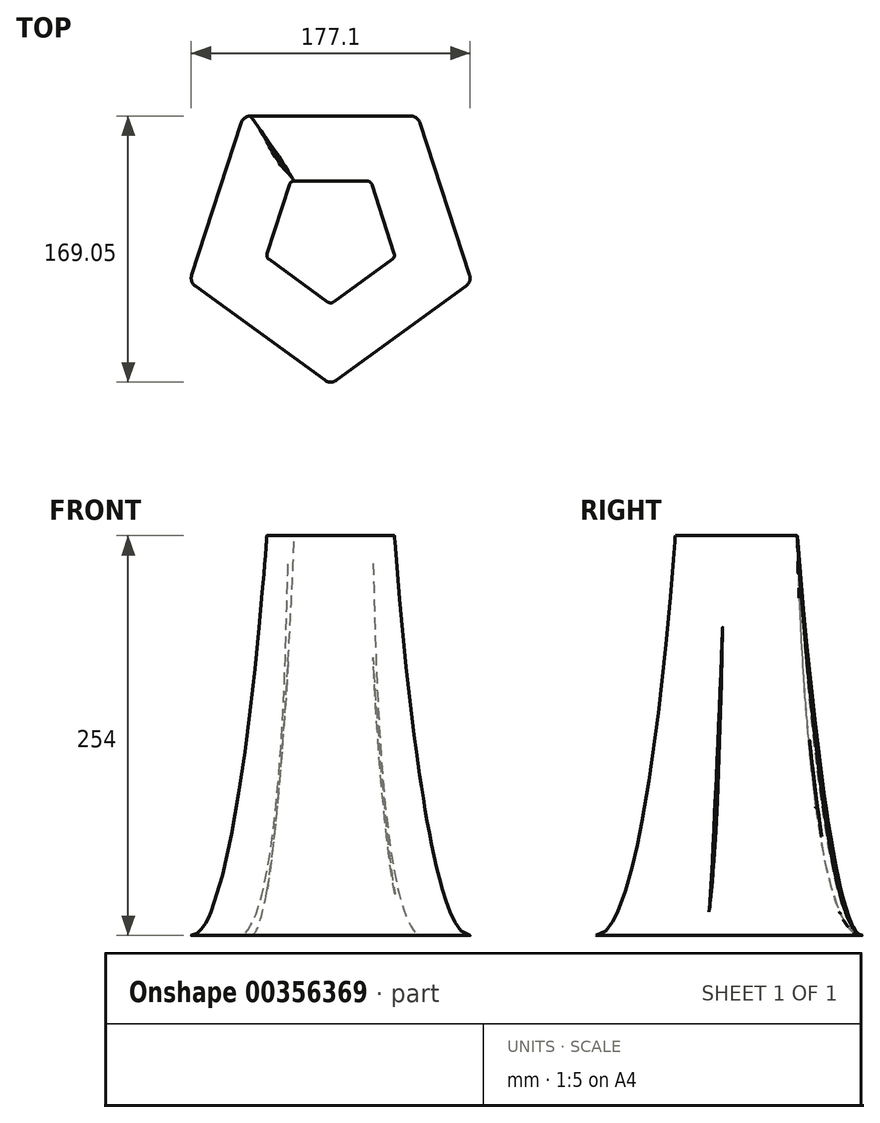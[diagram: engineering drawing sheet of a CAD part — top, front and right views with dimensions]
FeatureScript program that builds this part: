
annotation { "Feature Type Name" : "Feature", "Feature Type Description" : "" }
export const myFeature = defineFeature(function(context is Context, id is Id, definition is map)
    precondition{}
    {
        {
            var Q0;
            Q0=qCreatedBy(makeId("Top.planeOp"),FACE);
            var sketch = newSketch(context, id + "F0", { "sketchPlane" : qUnion([Q0])});
            skCircle(sketch, "E0.cCircle", {"center": v(0, 0) * mm, "radius": 76.27 * mm, "construction": true});
            skLineSegment(sketch, "E0.0", {"start": v(-50.8, 76.27) * mm, "end": v(50.8, 76.27) * mm});
            skLineSegment(sketch, "E0.1", {"start": v(56.84, 71.88) * mm, "end": v(88.24, -24.74) * mm});
            skLineSegment(sketch, "E0.2", {"start": v(85.93, -31.84) * mm, "end": v(3.73, -91.56) * mm});
            skLineSegment(sketch, "E0.3", {"start": v(-3.73, -91.56) * mm, "end": v(-85.93, -31.84) * mm});
            skLineSegment(sketch, "E0.4", {"start": v(-88.24, -24.74) * mm, "end": v(-56.84, 71.88) * mm});
            skPoint(sketch, "E0.0.midPoint", {"position": v(0, 76.27) * mm});
            skPoint(sketch, "E1.visualSharp", {"position": v(-55.41, 76.27) * mm});
            skArc(sketch, "E1.filletArc", {"start": v(-50.8, 76.27) * mm, "mid": v(-54.53, 75.06) * mm, "end": v(-56.84, 71.88) * mm});
            skPoint(sketch, "E2.visualSharp", {"position": v(55.41, 76.27) * mm});
            skArc(sketch, "E2.filletArc", {"start": v(56.84, 71.88) * mm, "mid": v(54.53, 75.06) * mm, "end": v(50.8, 76.27) * mm});
            skPoint(sketch, "E3.visualSharp", {"position": v(89.66, -29.13) * mm});
            skArc(sketch, "E3.filletArc", {"start": v(85.93, -31.84) * mm, "mid": v(88.24, -28.67) * mm, "end": v(88.24, -24.74) * mm});
            skPoint(sketch, "E4.visualSharp", {"position": v(-89.66, -29.13) * mm});
            skArc(sketch, "E4.filletArc", {"start": v(-88.24, -24.74) * mm, "mid": v(-88.24, -28.67) * mm, "end": v(-85.93, -31.84) * mm});
            skPoint(sketch, "E5.visualSharp", {"position": v(0, -94.28) * mm});
            skArc(sketch, "E5.filletArc", {"start": v(-3.73, -91.56) * mm, "mid": v(0, -92.78) * mm, "end": v(3.73, -91.56) * mm});
            skSolve(sketch);
        }
        {
            var Q0;
            Q0=makeQuery(id+"F0.imprint","IMPRINT",FACE,{"disambiguationData":[TD([[makeQuery(id+"F0.imprint","IMPRINT",EDGE,{"derivedFrom":sQuery(id+"F0.wireOp",EDGE,"E0.0")}),-1.0]])]});
            cPlane(context, id + "F1", {"entities" : qUnion([Q0]), "cplaneType" : CPlaneType.OFFSET, "offset" : 254 * mm, "width" : 152.4 * mm, "height" : 152.4 * mm});
        }
        {
            var Q0;
            Q0=qCreatedBy(id+"F1.planeOp",FACE);
            var sketch = newSketch(context, id + "F2", { "sketchPlane" : qUnion([Q0])});
            skCircle(sketch, "E6.cCircle", {"center": v(0, 0) * mm, "radius": 34.96 * mm, "construction": true});
            skLineSegment(sketch, "E6.0", {"start": v(-23.1, 34.96) * mm, "end": v(23.1, 34.96) * mm});
            skLineSegment(sketch, "E6.1", {"start": v(26.11, 32.77) * mm, "end": v(40.39, -11.16) * mm});
            skLineSegment(sketch, "E6.2", {"start": v(39.23, -14.7) * mm, "end": v(1.87, -41.86) * mm});
            skLineSegment(sketch, "E6.3", {"start": v(-1.87, -41.86) * mm, "end": v(-39.23, -14.7) * mm});
            skLineSegment(sketch, "E6.4", {"start": v(-40.39, -11.16) * mm, "end": v(-26.11, 32.77) * mm});
            skPoint(sketch, "E6.0.midPoint", {"position": v(0, 34.96) * mm});
            skPoint(sketch, "E7.visualSharp", {"position": v(-41.1, -13.35) * mm});
            skArc(sketch, "E7.filletArc", {"start": v(-40.39, -11.16) * mm, "mid": v(-40.39, -13.12) * mm, "end": v(-39.23, -14.7) * mm});
            skPoint(sketch, "E8.visualSharp", {"position": v(0, -43.21) * mm});
            skArc(sketch, "E8.filletArc", {"start": v(-1.87, -41.86) * mm, "mid": v(0, -42.46) * mm, "end": v(1.87, -41.86) * mm});
            skPoint(sketch, "E9.visualSharp", {"position": v(41.1, -13.35) * mm});
            skArc(sketch, "E9.filletArc", {"start": v(39.23, -14.7) * mm, "mid": v(40.39, -13.12) * mm, "end": v(40.39, -11.16) * mm});
            skPoint(sketch, "E10.visualSharp", {"position": v(25.4, 34.96) * mm});
            skArc(sketch, "E10.filletArc", {"start": v(26.11, 32.77) * mm, "mid": v(24.96, 34.35) * mm, "end": v(23.1, 34.96) * mm});
            skPoint(sketch, "E11.visualSharp", {"position": v(-25.4, 34.96) * mm});
            skArc(sketch, "E11.filletArc", {"start": v(-23.1, 34.96) * mm, "mid": v(-24.96, 34.35) * mm, "end": v(-26.11, 32.77) * mm});
            skSolve(sketch);
        }
        {
            var Q0;
            Q0=makeQuery(id+"F0.imprint","IMPRINT",FACE,{"disambiguationData":[TD([[makeQuery(id+"F0.imprint","IMPRINT",EDGE,{"derivedFrom":sQuery(id+"F0.wireOp",EDGE,"E0.0")}),-1.0]])]});
            var Q1;
            Q1=makeQuery(id+"F2.imprint","IMPRINT",FACE,{"disambiguationData":[TD([[makeQuery(id+"F2.imprint","IMPRINT",EDGE,{"derivedFrom":sQuery(id+"F2.wireOp",EDGE,"E6.0")}),-1.0]])]});
            loft(context, id + "F3", {"sheetProfilesArray" : [{ "sheetProfileEntities" : qUnion([Q0]) }, { "sheetProfileEntities" : qUnion([Q1]) }], "startCondition" : LoftEndDerivativeType.TANGENT_TO_PROFILE, "startMagnitude" : 2, "endCondition" : LoftEndDerivativeType.TANGENT_TO_PROFILE, "endMagnitude" : 0});
        }
    });
